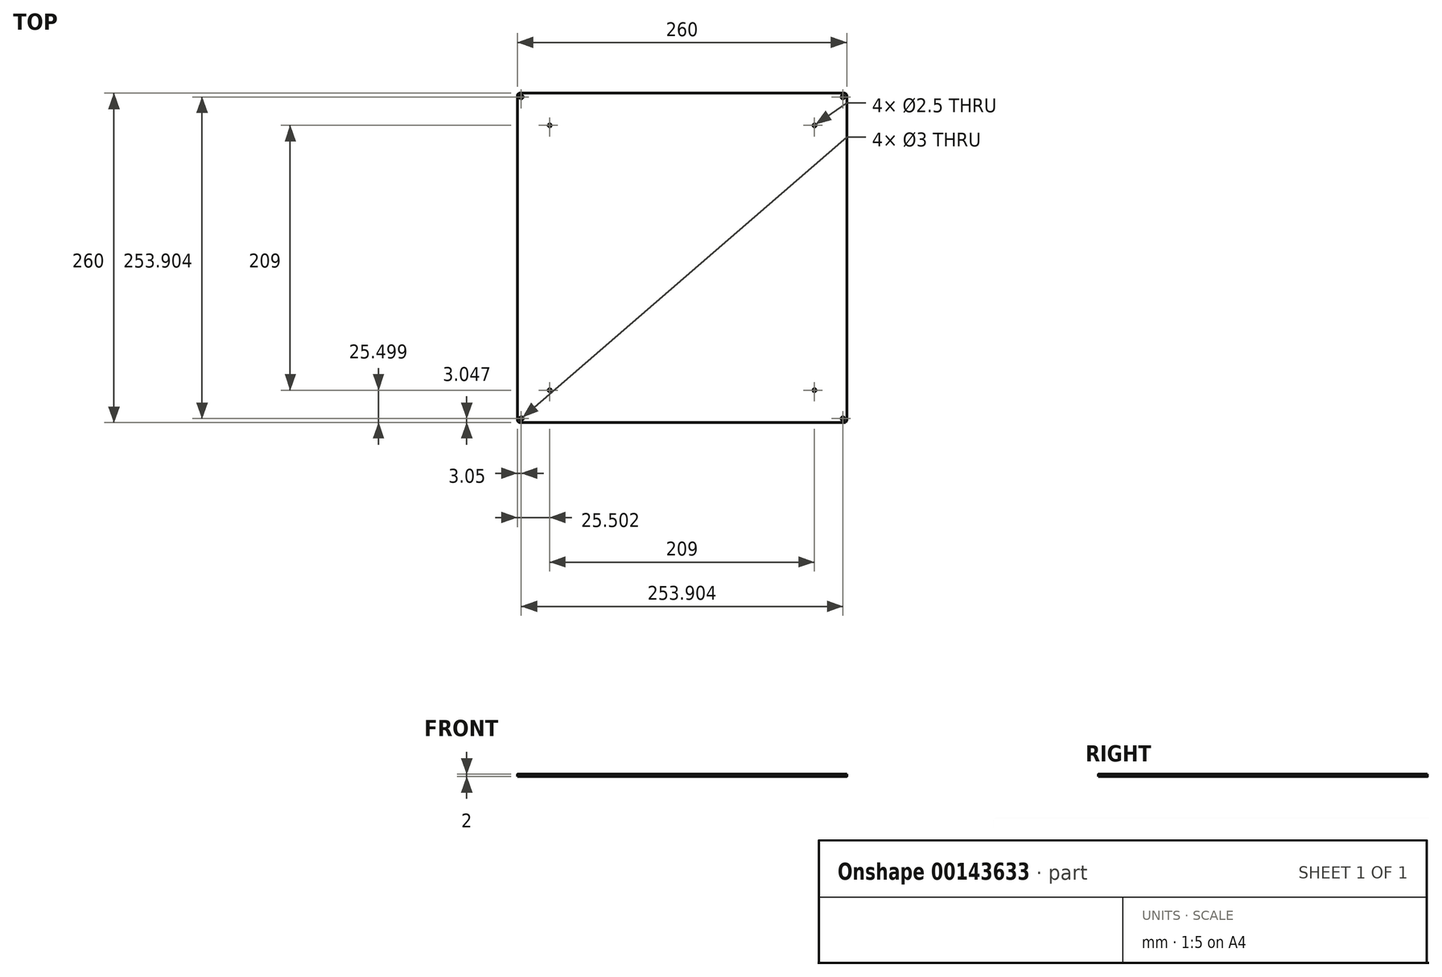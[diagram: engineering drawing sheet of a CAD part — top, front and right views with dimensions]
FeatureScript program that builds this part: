
annotation { "Feature Type Name" : "Feature", "Feature Type Description" : "" }
export const myFeature = defineFeature(function(context is Context, id is Id, definition is map)
    precondition{}
    {
        {
            var Q0;
            Q0=qCreatedBy(makeId("Top.planeOp"),FACE);
            var sketch = newSketch(context, id + "F0", { "sketchPlane" : qUnion([Q0])});
            skCircle(sketch, "E0", {"center": v(0, 0) * mm, "radius": 4 * mm});
            skLineSegment(sketch, "E1.bottom", {"start": v(117.25, 114.2) * mm, "end": v(373.25, 114.2) * mm});
            skLineSegment(sketch, "E1.top", {"start": v(117.25, 374.2) * mm, "end": v(373.25, 374.2) * mm});
            skLineSegment(sketch, "E1.left", {"start": v(115.25, 116.2) * mm, "end": v(115.25, 372.2) * mm});
            skLineSegment(sketch, "E1.right", {"start": v(375.25, 116.2) * mm, "end": v(375.25, 372.2) * mm});
            skLineSegment(sketch, "E2.bottom", {"start": v(349.75, 348.7) * mm, "end": v(140.75, 348.7) * mm, "construction": true});
            skLineSegment(sketch, "E2.top", {"start": v(349.75, 139.7) * mm, "end": v(140.75, 139.7) * mm, "construction": true});
            skLineSegment(sketch, "E2.left", {"start": v(349.75, 348.7) * mm, "end": v(349.75, 139.7) * mm, "construction": true});
            skLineSegment(sketch, "E2.right", {"start": v(140.75, 348.7) * mm, "end": v(140.75, 139.7) * mm, "construction": true});
            skPoint(sketch, "E2.middle", {"position": v(245.25, 244.2) * mm});
            skPoint(sketch, "E2.middle.positionSnap0", {"position": v(245.25, 114.2) * mm});
            skPoint(sketch, "E2.middle.positionSnap1", {"position": v(115.25, 244.2) * mm});
            skPoint(sketch, "E2.centerSnap0", {"position": v(245.25, 114.2) * mm});
            skPoint(sketch, "E2.centerSnap1", {"position": v(115.25, 244.2) * mm});
            skCircle(sketch, "E3", {"center": v(140.75, 139.7) * mm, "radius": 1.25 * mm});
            skCircle(sketch, "E4", {"center": v(140.75, 348.7) * mm, "radius": 1.25 * mm});
            skCircle(sketch, "E5", {"center": v(349.75, 139.7) * mm, "radius": 1.25 * mm});
            skCircle(sketch, "E6", {"center": v(349.75, 348.7) * mm, "radius": 1.25 * mm});
            skLineSegment(sketch, "E7.0", {"start": v(120.25, 119.2) * mm, "end": v(120.25, 369.2) * mm, "construction": true});
            skLineSegment(sketch, "E7.1", {"start": v(120.25, 119.2) * mm, "end": v(370.25, 119.2) * mm, "construction": true});
            skLineSegment(sketch, "E7.2", {"start": v(370.25, 119.2) * mm, "end": v(370.25, 369.2) * mm, "construction": true});
            skLineSegment(sketch, "E7.3", {"start": v(120.25, 369.2) * mm, "end": v(370.25, 369.2) * mm, "construction": true});
            skLineSegment(sketch, "E8", {"start": v(115.25, 114.2) * mm, "end": v(120.25, 119.2) * mm, "construction": true});
            skCircle(sketch, "E9", {"center": v(118.3, 117.25) * mm, "radius": 1.5 * mm});
            skLineSegment(sketch, "E10", {"start": v(375.25, 244.2) * mm, "end": v(266.34, 244.2) * mm, "construction": true});
            skLineSegment(sketch, "E11", {"start": v(245.25, 374.2) * mm, "end": v(245.25, 283.74) * mm, "construction": true});
            skCircle(sketch, "E12.MirrorC", {"center": v(372.2, 117.25) * mm, "radius": 1.5 * mm});
            skCircle(sketch, "E13.MirrorC", {"center": v(372.2, 371.15) * mm, "radius": 1.5 * mm});
            skCircle(sketch, "E14.MirrorC", {"center": v(118.3, 371.15) * mm, "radius": 1.5 * mm});
            skCircle(sketch, "E15", {"center": v(118.3, 117.25) * mm, "radius": 2.76 * mm, "construction": true});
            skPoint(sketch, "E16.visualSharp", {"position": v(115.25, 114.2) * mm});
            skArc(sketch, "E16.filletArc", {"start": v(115.25, 116.2) * mm, "mid": v(115.84, 114.79) * mm, "end": v(117.25, 114.2) * mm});
            skPoint(sketch, "E17.visualSharp", {"position": v(115.25, 374.2) * mm});
            skArc(sketch, "E17.filletArc", {"start": v(117.25, 374.2) * mm, "mid": v(115.84, 373.61) * mm, "end": v(115.25, 372.2) * mm});
            skPoint(sketch, "E18.visualSharp", {"position": v(375.25, 374.2) * mm});
            skArc(sketch, "E18.filletArc", {"start": v(375.25, 372.2) * mm, "mid": v(374.67, 373.61) * mm, "end": v(373.25, 374.2) * mm});
            skPoint(sketch, "E19.visualSharp", {"position": v(375.25, 114.2) * mm});
            skArc(sketch, "E19.filletArc", {"start": v(373.25, 114.2) * mm, "mid": v(374.67, 114.79) * mm, "end": v(375.25, 116.2) * mm});
            skSolve(sketch);
        }
        {
            var Q0;
            Q0=makeQuery(id+"F0.imprint","IMPRINT",FACE,{"disambiguationData":[TD([[makeQuery(id+"F0.imprint","IMPRINT",EDGE,{"derivedFrom":sQuery(id+"F0.wireOp",EDGE,"E1.bottom")}),1.0]])]});
            extrude(context, id + "F1", {"entities" : qUnion([Q0]), "depth" : 2 * mm});
        }
    });
